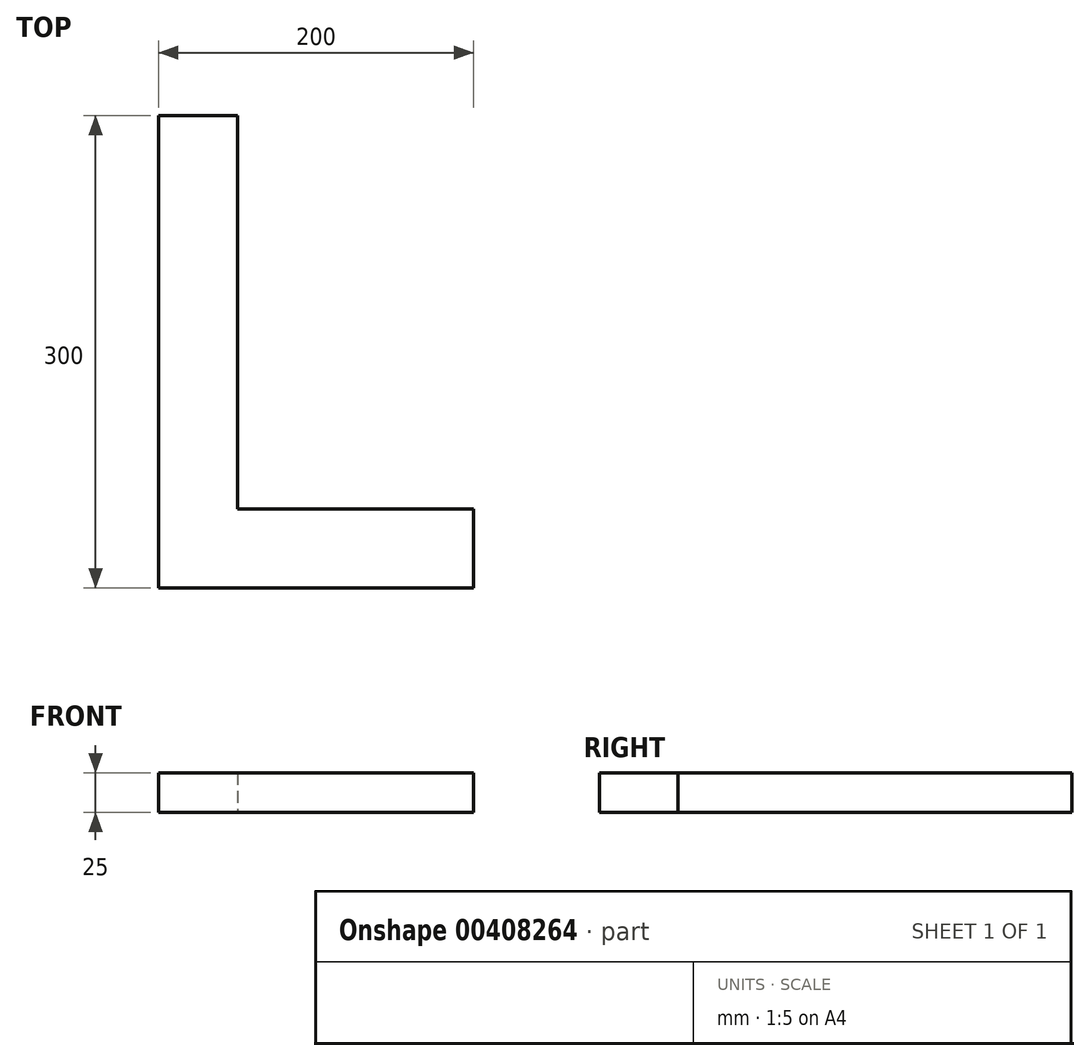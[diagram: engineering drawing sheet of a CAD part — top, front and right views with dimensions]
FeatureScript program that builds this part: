
annotation { "Feature Type Name" : "Feature", "Feature Type Description" : "" }
export const myFeature = defineFeature(function(context is Context, id is Id, definition is map)
    precondition{}
    {
        {
            var Q0;
            Q0=qCreatedBy(makeId("Top.planeOp"),FACE);
            var sketch = newSketch(context, id + "F0", { "sketchPlane" : qUnion([Q0])});
            skLineSegment(sketch, "E0.bottom", {"start": v(-50, -150) * mm, "end": v(-100, -150) * mm});
            skLineSegment(sketch, "E0.top", {"start": v(-50, 150) * mm, "end": v(-100, 150) * mm});
            skLineSegment(sketch, "E0.left", {"start": v(-50, -150) * mm, "end": v(-50, 150) * mm});
            skLineSegment(sketch, "E0.right", {"start": v(-100, -150) * mm, "end": v(-100, 150) * mm});
            skPoint(sketch, "E0.middle", {"position": v(-75, 0) * mm});
            skLineSegment(sketch, "E1.bottom", {"start": v(-100, -150) * mm, "end": v(100, -150) * mm});
            skLineSegment(sketch, "E1.top", {"start": v(-100, -100) * mm, "end": v(100, -100) * mm});
            skLineSegment(sketch, "E1.left", {"start": v(-100, -150) * mm, "end": v(-100, -100) * mm});
            skLineSegment(sketch, "E1.right", {"start": v(100, -150) * mm, "end": v(100, -100) * mm});
            skPoint(sketch, "E1.middle", {"position": v(0, -125) * mm});
            skSolve(sketch);
        }
        {
            var Q0;
            Q0 = qSketchRegion(id + "F0", true);
            extrude(context, id + "F1", {"entities" : qUnion([Q0]), "depth" : 25 * mm});
        }
    });
